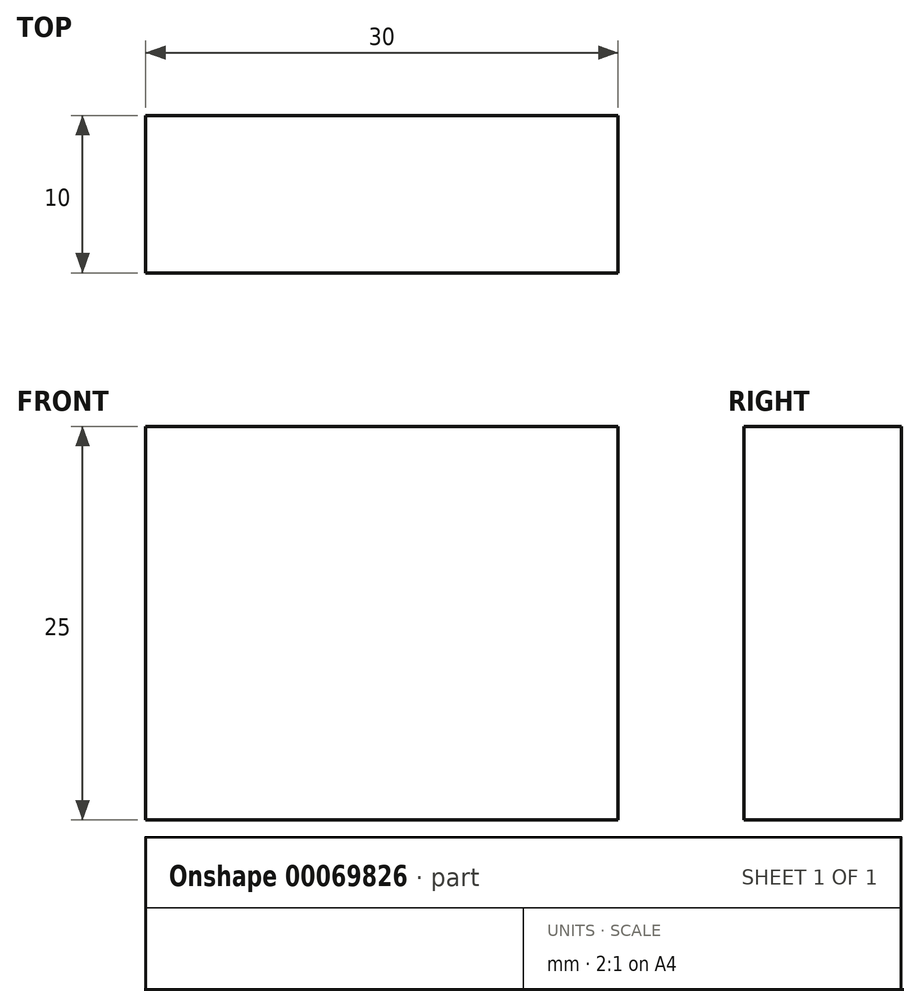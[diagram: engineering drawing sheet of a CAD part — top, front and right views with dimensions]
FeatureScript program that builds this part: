
annotation { "Feature Type Name" : "Feature", "Feature Type Description" : "" }
export const myFeature = defineFeature(function(context is Context, id is Id, definition is map)
    precondition{}
    {
        {
            var Q0;
            Q0=qCreatedBy(makeId("Top.planeOp"),FACE);
            var sketch = newSketch(context, id + "F0", { "sketchPlane" : qUnion([Q0])});
            skLineSegment(sketch, "E0.bottom", {"start": v(-15, -5) * mm, "end": v(15, -5) * mm});
            skLineSegment(sketch, "E0.top", {"start": v(-15, 5) * mm, "end": v(15, 5) * mm});
            skLineSegment(sketch, "E0.left", {"start": v(-15, -5) * mm, "end": v(-15, 5) * mm});
            skLineSegment(sketch, "E0.right", {"start": v(15, -5) * mm, "end": v(15, 5) * mm});
            skPoint(sketch, "E0.middle", {"position": v(0, 0) * mm});
            skSolve(sketch);
        }
        {
            var Q0;
            Q0=makeQuery(id+"F0.imprint","IMPRINT",FACE,{"disambiguationData":[TD([[makeQuery(id+"F0.imprint","IMPRINT",EDGE,{"derivedFrom":sQuery(id+"F0.wireOp",EDGE,"E0.bottom")}),1.0]])]});
            extrude(context, id + "F1", {"entities" : qUnion([Q0]), "depth" : 25 * mm, "offsetDistance" : 25 * mm});
        }
    });
